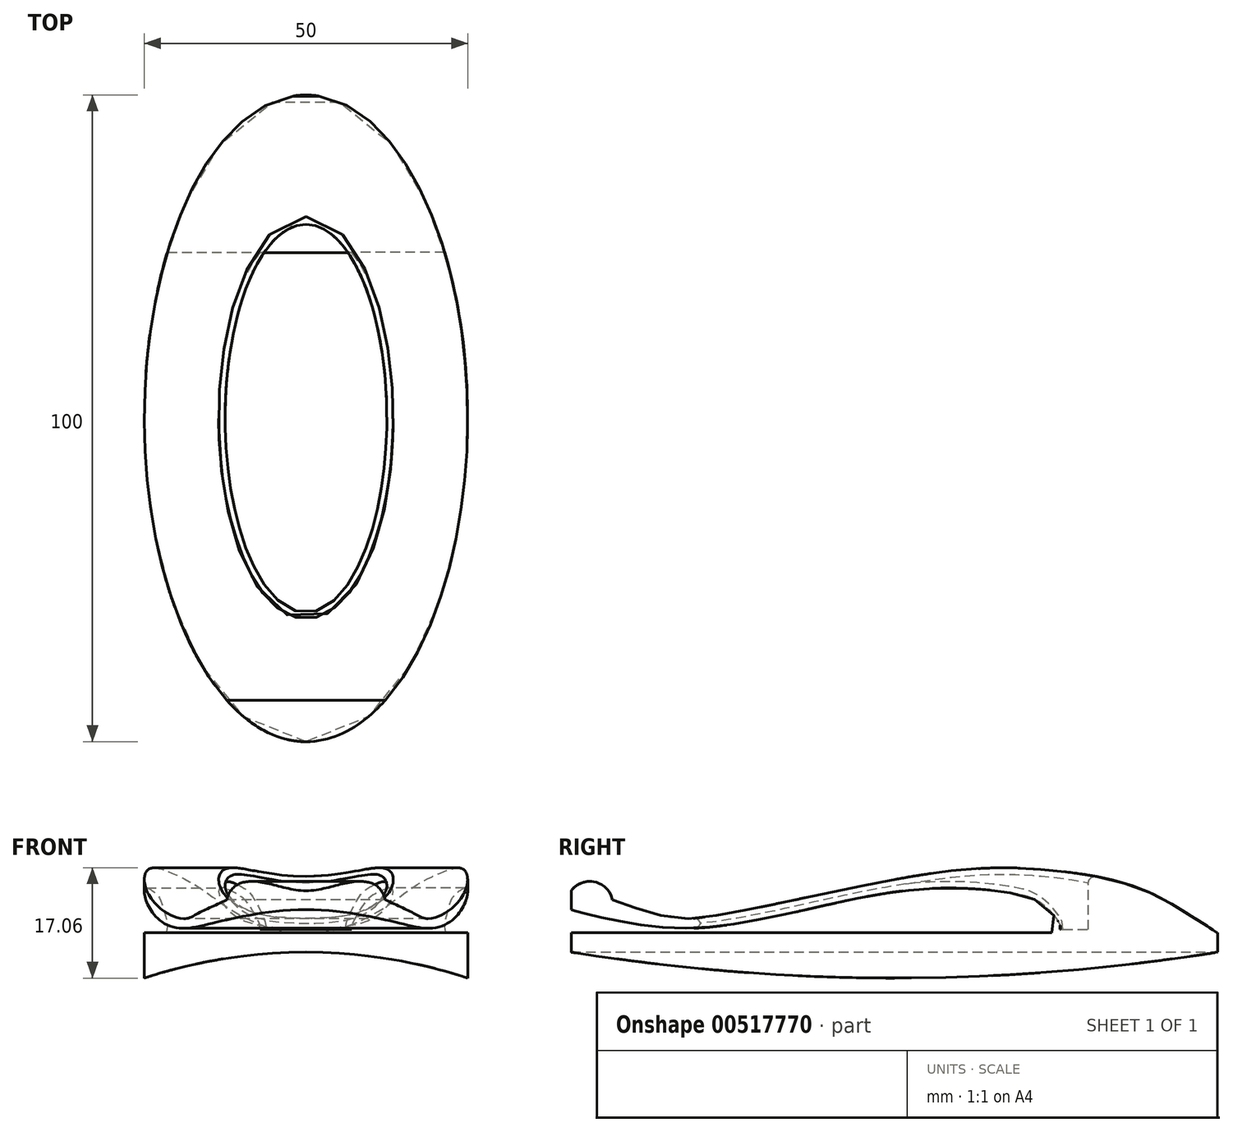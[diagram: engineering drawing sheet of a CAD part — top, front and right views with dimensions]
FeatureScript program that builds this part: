
annotation { "Feature Type Name" : "Feature", "Feature Type Description" : "" }
export const myFeature = defineFeature(function(context is Context, id is Id, definition is map)
    precondition{}
    {
        {
            assignVariable(context, id + "F0", {"name" : "baseWidth", "anyValue" : 50});
        }
        {
            var Q0;
            Q0=qCreatedBy(makeId("Top.planeOp"),FACE);
            var sketch = newSketch(context, id + "F1", { "sketchPlane" : qUnion([Q0])});
            skLineSegment(sketch, "E0.bottom", {"start": v(-25, 50) * mm, "end": v(25, 50) * mm});
            skLineSegment(sketch, "E0.top", {"start": v(-25, -50) * mm, "end": v(25, -50) * mm});
            skLineSegment(sketch, "E0.left", {"start": v(-25, 50) * mm, "end": v(-25, -50) * mm});
            skLineSegment(sketch, "E0.right", {"start": v(25, 50) * mm, "end": v(25, -50) * mm});
            skPoint(sketch, "E0.middle", {"position": v(0, 0) * mm});
            skSolve(sketch);
        }
        {
            var Q0;
            Q0=qSketchRegion(id+"F1",true);
            extrude(context, id + "F2", {"entities" : qUnion([Q0]), "oppositeDirection" : true, "depth" : 9 * mm});
        }
        {
            var Q0;
            Q0=qCreatedBy(makeId("Front.planeOp"),FACE);
            var sketch = newSketch(context, id + "F3", { "sketchPlane" : qUnion([Q0])});
            skLineSegment(sketch, "E1", {"start": v(0, 0) * mm, "end": v(0, -3) * mm, "construction": true});
            skLineSegment(sketch, "E2", {"start": v(0, -3) * mm, "end": v(0, -83) * mm, "construction": true});
            skPoint(sketch, "E3.MirrorCS.end.orphan", {"position": v(27.63, -4.62) * mm});
            skPoint(sketch, "E3.MirrorCS.start.orphan", {"position": v(0, 0) * mm});
            skPoint(sketch, "E4.MirrorCS.end.orphan", {"position": v(25.3, -9.1) * mm});
            skPoint(sketch, "E5.start.orphan", {"position": v(-27.63, -4.62) * mm});
            skPoint(sketch, "E6.end.orphan", {"position": v(-25.3, -9.1) * mm});
            skPoint(sketch, "E7.MirrorCS.start.orphan", {"position": v(0, -3) * mm});
            skCircle(sketch, "E8", {"center": v(0, -83) * mm, "radius": 80 * mm});
            skSolve(sketch);
        }
        {
            var Q0;
            Q0=qSketchRegion(id+"F3",true);
            extrude(context, id + "F4", {"entities" : qUnion([Q0]), "operationType" : NewBodyOperationType.REMOVE, "depth" : 58.6 * mm, "hasSecondDirection" : true, "secondDirectionOppositeDirection" : true, "secondDirectionDepth" : 93.1 * mm});
        }
        {
            var Q0;
            Q0=qSketchRegion(id+"F3",true);
            extrude(context, id + "F5", {"entities" : qUnion([Q0]), "operationType" : NewBodyOperationType.REMOVE, "depth" : 59.3 * mm, "hasSecondDirection" : true, "secondDirectionOppositeDirection" : true, "secondDirectionDepth" : 67.2 * mm});
        }
        {
            var Q0;
            Q0=qCreatedBy(makeId("Right.planeOp"),FACE);
            var sketch = newSketch(context, id + "F6", { "sketchPlane" : qUnion([Q0])});
            skLineSegment(sketch, "E9", {"start": v(0, 0) * mm, "end": v(70.45, 0) * mm, "construction": true});
            skFitSpline(sketch, "E10", {"points": [v(49.84, 0) * mm, v(45.5, 2.82) * mm, v(37.77, 6.91) * mm, v(25.1, 9.58) * mm, v(4.82, 9.05) * mm, v(-31.53, 2.2) * mm, v(-37.07, 2.96) * mm, v(-43.6, 5.1) * mm], "startDerivative": vector(-43.63, 31.79) * mm, "endDerivative": vector(-64.7, 27.4) * mm});
            skFitSpline(sketch, "E11", {"points": [v(24.33, 0) * mm, v(23.88, 3.52) * mm, v(18.73, 6.05) * mm, v(7.22, 6.9) * mm, v(-8.3, 4.78) * mm, v(-30.23, 0.75) * mm, v(-42.88, 1.88) * mm, v(-50.65, 3.78) * mm], "startDerivative": vector(92.2, 0) * mm, "endDerivative": vector(-63.45, 20.53) * mm});
            skArc(sketch, "E12", {"start": v(-43.6, 5.1) * mm, "mid": v(-47.78, 7.89) * mm, "end": v(-50.65, 3.78) * mm});
            skPoint(sketch, "E12.third.point", {"position": v(-49.52, 7.02) * mm});
            skArc(sketch, "E13", {"start": v(24.33, 0) * mm, "mid": v(37.09, -2.93) * mm, "end": v(49.84, 0) * mm});
            skSolve(sketch);
        }
        {
            var Q0;
            {var subQ1=sQuery(id+"F6.wireOp",EDGE,"E10");Q0=makeQuery(id+"F6.imprint","IMPRINT",FACE,{"disambiguationData":[TD([[makeQuery(id+"F6.imprint","IMPRINT",EDGE,{"derivedFrom":subQ1}),1.0]])]});}
            extrude(context, id + "F7", {"entities" : qUnion([Q0]), "depth" : (getVariable(context, 'baseWidth') / 2) * mm, "hasSecondDirection" : true, "secondDirectionOppositeDirection" : true, "secondDirectionDepth" : (getVariable(context, 'baseWidth') / 2) * mm});
        }
        {
            var Q0;
            Q0=qCreatedBy(makeId("Top.planeOp"),FACE);
            var sketch = newSketch(context, id + "F8", { "sketchPlane" : qUnion([Q0])});
            skEllipse(sketch, "E14", {"center": v(0, 0) * mm, "majorRadius": 30 * mm, "minorRadius": 12.5 * mm, "majorAxis": v(0, 1)});
            skSolve(sketch);
        }
        {
            var Q0;
            Q0=qSketchRegion(id+"F8",true);
            extrude(context, id + "F9", {"entities" : qUnion([Q0]), "operationType" : NewBodyOperationType.REMOVE, "depth" : 23.9 * mm, "hasSecondDirection" : true, "secondDirectionOppositeDirection" : false, "secondDirectionDepth" : 0.5 * mm});
        }
        {
            var Q0;
            Q0=qCreatedBy(makeId("Top.planeOp"),FACE);
            var sketch = newSketch(context, id + "F10", { "sketchPlane" : qUnion([Q0])});
            skEllipse(sketch, "E15", {"center": v(0, 0) * mm, "majorRadius": 50 * mm, "minorRadius": 25 * mm, "majorAxis": v(0, -1)});
            skSolve(sketch);
        }
        {
            var Q0;
            Q0=qSketchRegion(id+"F10",true);
            extrude(context, id + "F11", {"entities" : qUnion([Q0]), "operationType" : NewBodyOperationType.INTERSECT, "oppositeDirection" : true, "depth" : 25 * mm, "hasSecondDirection" : true, "secondDirectionOppositeDirection" : false, "secondDirectionDepth" : 25 * mm});
        }
        {
            var Q0;
            Q0=makeQuery(id+"F2.opExtrude","SWEPT_BODY",BODY,{"disambiguationData":[OSD([sQuery(id+"F1.wireOp",EDGE,"E0.bottom"),sQuery(id+"F1.wireOp",EDGE,"E0.top"),sQuery(id+"F1.wireOp",EDGE,"E0.left"),sQuery(id+"F1.wireOp",EDGE,"E0.right")])]});
            var Q1;
            Q1=makeQuery(id+"F7.opExtrude","SWEPT_BODY",BODY,{"disambiguationData":[OSD([sQuery(id+"F6.wireOp",EDGE,"E10"),sQuery(id+"F6.wireOp",EDGE,"E11"),sQuery(id+"F6.wireOp",EDGE,"E12"),sQuery(id+"F6.wireOp",EDGE,"E13")])]});
            booleanBodies(context, id + "F12", {"operationType" : BooleanOperationType.UNION, "tools" : qUnion([Q0, Q1])});
        }
        {
            var Q0;
            Q0=makeQuery(id+"F11.boolean.opBoolean","INTERSECT",EDGE,{"disambiguationData":[OD(1.0)],"derivedFrom":[makeQuery(id+"F7.opExtrude","SWEPT_FACE",FACE,{"disambiguationData":[OSD([sQuery(id+"F6.wireOp",EDGE,"E10")])]}),makeQuery(id+"F11.boolean.toolComplement.opBoolean","COPY",FACE,{"derivedFrom":makeQuery(id+"F11.opExtrude","SWEPT_FACE",FACE,{"disambiguationData":[OSD([sQuery(id+"F10.wireOp",EDGE,"E15")])]})})]});
            var Q1;
            Q1=makeQuery(id+"F9.boolean.opBoolean","INTERSECT",EDGE,{"derivedFrom":[makeQuery(id+"F7.opExtrude","SWEPT_FACE",FACE,{"disambiguationData":[OSD([sQuery(id+"F6.wireOp",EDGE,"E10")])]}),makeQuery(id+"F9.opExtrude","SWEPT_FACE",FACE,{"disambiguationData":[OSD([sQuery(id+"F8.wireOp",EDGE,"E14")])]})]});
            var Q2;
            Q2=makeQuery(id+"F11.boolean.opBoolean","INTERSECT",EDGE,{"derivedFrom":[makeQuery(id+"F7.opExtrude","SWEPT_FACE",FACE,{"disambiguationData":[OSD([sQuery(id+"F6.wireOp",EDGE,"E12")])]}),makeQuery(id+"F11.boolean.toolComplement.opBoolean","COPY",FACE,{"derivedFrom":makeQuery(id+"F11.opExtrude","SWEPT_FACE",FACE,{"disambiguationData":[OSD([sQuery(id+"F10.wireOp",EDGE,"E15")])]})})]});
            var Q3;
            {var subQ0=sQuery(id+"F1.wireOp",EDGE,"E0.right");var subQ1=sQuery(id+"F1.wireOp",EDGE,"E0.left");var subQ2=sQuery(id+"F1.wireOp",EDGE,"E0.top");var subQ3=sQuery(id+"F1.wireOp",EDGE,"E0.bottom");var subQ4=makeQuery(id+"F2.opExtrude","CAP_FACE",FACE,{"disambiguationData":[OSD([subQ3,subQ2,subQ1,subQ0])],"isStart":true});var subQ5=makeQuery(id+"F7.opExtrude","SWEPT_FACE",FACE,{"disambiguationData":[OSD([sQuery(id+"F6.wireOp",EDGE,"E11")])]});var subQ6=makeQuery(id+"F11.boolean.toolComplement.opBoolean","COPY",FACE,{"derivedFrom":makeQuery(id+"F11.opExtrude","SWEPT_FACE",FACE,{"disambiguationData":[OSD([sQuery(id+"F10.wireOp",EDGE,"E15")])]})});Q3=makeQuery(id+"F12.opBoolean","SPLIT",EDGE,{"disambiguationData":[TD([subQ5])],"derivedFrom":makeQuery(id+"F11.boolean.opBoolean","INTERSECT",EDGE,{"derivedFrom":[subQ4,subQ6]})});}
            var Q4;
            Q4=makeQuery(id+"F9.boolean.opBoolean","INTERSECT",EDGE,{"derivedFrom":[makeQuery(id+"F7.opExtrude","SWEPT_FACE",FACE,{"disambiguationData":[OSD([sQuery(id+"F6.wireOp",EDGE,"E11")])]}),makeQuery(id+"F9.opExtrude","SWEPT_FACE",FACE,{"disambiguationData":[OSD([sQuery(id+"F8.wireOp",EDGE,"E14")])]})]});
            var Q5;
            Q5=makeQuery(id+"F11.boolean.opBoolean","INTERSECT",EDGE,{"derivedFrom":[makeQuery(id+"F4.boolean.opBoolean","COPY",FACE,{"derivedFrom":makeQuery(id+"F4.opExtrude","SWEPT_FACE",FACE,{"disambiguationData":[OSD([sQuery(id+"F3.wireOp",EDGE,"E8")])]})}),makeQuery(id+"F11.boolean.toolComplement.opBoolean","COPY",FACE,{"derivedFrom":makeQuery(id+"F11.opExtrude","SWEPT_FACE",FACE,{"disambiguationData":[OSD([sQuery(id+"F10.wireOp",EDGE,"E15")])]})})]});
            fillet(context, id + "F13", {"entities" : qUnion([Q0, Q1, Q2, Q3, Q4, Q5]), "radius" : 1 * mm, "tangentPropagation" : true, "allowEdgeOverflow" : false});
        }
    });
